# Revit family: ToiletRollHolder_SurfaceMount_Nero_Dolce
name_source: partatom
category: Specialty Equipment
units: mm (PartAtom-declared; Revit-internal decimal feet)

## family parameters
Always vertical = Yes
Cut with Voids When Loaded = No
Maintain Annotation Orientation = No
OmniClass Number = 23.31.25.27
Part Type = Normal
Room Calculation Point = No
Round Connector Dimension = Use Diameter
Shared = No
Work Plane-Based = No

## types (3) — shared parameters
Assembly Code = C1030210
IfcExportAs = IfcFurniture
IfcExportType = NOTDEFINED
Manufacturer = Nero
ManufacturerOverallDepth = 91.5 mm
ManufacturerOverallHeight = 52 mm  [stored 0.170604 ft]
ManufacturerOverallWidth = 159.5 mm  [stored 0.523294 ft]
ManufacturerURLProductSpecific = https://nerotapware.com.au
ModifiedIssue = 20241210 $
URL = https://nerotapware.com.au
Uniclass2015Code = Pr_40_70_22_61
Uniclass2015Title = Paper roll dispensers
Uniclass2015Version = Products v1.35
zero-valued in all types: Default Elevation

## per-type parameters (varying)
| type | BodyMaterial | Description | ManufacturerSpecCode | Model | Type Comments |
| Brushed Nickel (NR3686wBN) | Metal_Nickel_Nero_Brushed | Dolce Toilet Roll Holder Brushed Nickel | NR3686wBN | NR3686wBN | Toilet Roll Holder - Surface Mount - Brushed Nickel |
| Matte Black (NR3686wMB) | Metal_MatteBlack_Nero | Dolce Toilet Roll Holder Matte Black | NR3686wMB | NR3686wMB | Toilet Roll Holder - Surface Mount - Matte Black |
| Chrome (NR3686wCH) | Metal_Chrome_Nero | Dolce Toilet Roll Holder Chrome | NR3686wCH | NR3686wCH | Toilet Roll Holder - Surface Mount - Chrome |

note: [stored X ft] marks values corroborated as IEEE doubles in the binary element streams (Revit-internal decimal feet)

## geometry (parser evidence)
native form markers: Sweep x3
no freeform markers — native parametric forms only
